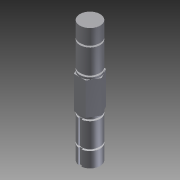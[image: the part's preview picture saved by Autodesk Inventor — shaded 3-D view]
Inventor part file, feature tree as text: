
AUTODESK INVENTOR PART (.ipt)
format: ipt  version: 2012 (Build 160160000, 160)  size: 147,968 bytes
history: native  units: in
note: dims shown in document units (in); Inventor stores cm internally (conversion verified against a paired STEP export)
features: sketch x3, other x1, extrude x1, imported_body x1
ambient origin geometry x8: Origin, YZ Plane, XZ Plane, XY Plane, X Axis, Y Axis, Z Axis, Center Point
bodies: Solid1 (feature_tree)
feature tree (6):
  other  "wheel shaft.CATPart1"
  sketch  "3D Sketch2"
  extrude  "Extrusion1"  TaperAngle=0.0deg  [1 undecoded]
  sketch  "3D Sketch1"
  imported_body  "Base1"
  sketch  "Sketch1"  dims[d1=0.0in d2=0.0in d3=0.0787in d4=0.2106in d5=0.0394in d6=0.0in]
note: 1 required parameter value undecoded (feature->parameter linkage not recoverable at this tier; creation-order binding heuristic only, values carry confidence <= 0.55)
